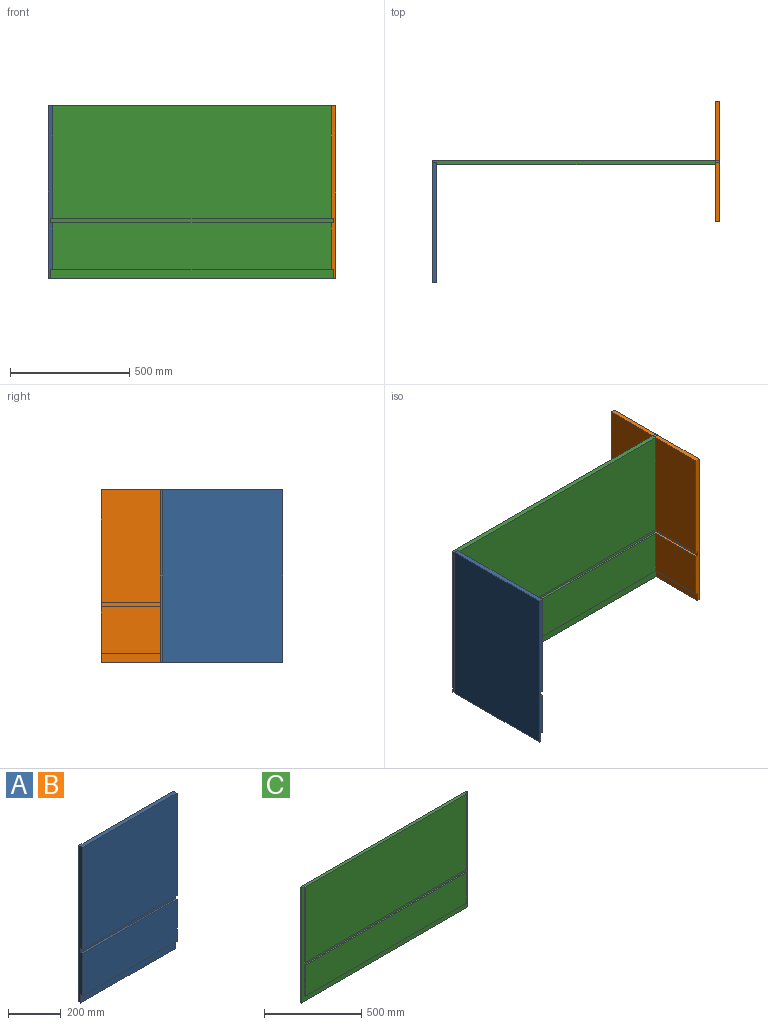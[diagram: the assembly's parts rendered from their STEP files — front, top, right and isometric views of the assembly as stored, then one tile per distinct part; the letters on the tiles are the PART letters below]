
ASSEMBLY  parts=3 mates=4
PART A: 12 faces, bbox 504.8x19.1x723.9 mm
  f0: plane 504.83x9.53mm, normal (0,0,-1), area 4808.5mm2, adj f3,f5,f6,f11
  f1: plane 504.83x473.08mm, normal (0,-1,0), area 238820.1mm2, adj f3,f4,f5,f8
  f2: plane 504.83x193.68mm, normal (0,-1,0), area 97772mm2, adj f3,f5,f7,f10
  f3: plane 723.9x19.05mm, normal (1,0,0), area 13245.9mm2, adj f0,f1,f2,f4,f6,f7,f8,f9
  f4: plane 504.83x19.05mm, normal (0,0,1), area 9616.9mm2, adj f1,f3,f5,f6
  f5: plane 723.9x19.05mm, normal (-1,0,0), area 13245.9mm2, adj f0,f1,f2,f4,f6,f7,f8,f9
  f6: plane 723.9x504.83mm, normal (0,1,0), area 365442.8mm2, adj f0,f3,f4,f5
  f7: plane 504.83x9.53mm, normal (0,0,1), area 4808.5mm2, adj f2,f3,f5,f9
  f8: plane 504.83x9.53mm, normal (0,0,-1), area 4808.5mm2, adj f1,f3,f5,f9
  f9: plane 504.83x19.05mm, normal (0,-1,0), area 9616.9mm2, adj f3,f5,f7,f8
  f10: plane 504.83x9.53mm, normal (0,0,-1), area 4808.5mm2, adj f2,f3,f5,f11
  f11: plane 504.83x38.1mm, normal (0,-1,0), area 19233.8mm2, adj f0,f3,f5,f10
PART B: same geometry as A
PART C: 15 faces, bbox 1206.5x19.1x723.9 mm
  f0: plane 723.9x9.53mm, normal (1,0,0), area 6895.1mm2, adj f2,f3,f5,f13
  f1: plane 723.9x9.53mm, normal (-1,0,0), area 6895.1mm2, adj f2,f3,f5,f13
  f2: plane 1206.5x9.53mm, normal (0,0,-1), area 11491.9mm2, adj f0,f1,f5,f13
  f3: plane 1206.5x19.05mm, normal (0,0,1), area 22620.9mm2, adj f0,f1,f4,f5,f9,f11,f13
  f4: plane 1168.4x473.08mm, normal (0,-1,0), area 552740.8mm2, adj f3,f9,f10,f11
  f5: plane 1206.5x723.9mm, normal (0,1,0), area 873385.3mm2, adj f0,f1,f2,f3
  f6: plane 1168.4x9.53mm, normal (0,0,-1), area 11129mm2, adj f7,f12,f13,f14
  f7: plane 193.68x9.53mm, normal (-1,0,0), area 1844.8mm2, adj f6,f8,f13,f14
  f8: plane 1168.4x9.53mm, normal (0,0,1), area 11129mm2, adj f7,f12,f13,f14
  f9: plane 473.08x9.53mm, normal (1,0,0), area 4506mm2, adj f3,f4,f10,f13
  f10: plane 1168.4x9.53mm, normal (0,0,-1), area 11129mm2, adj f4,f9,f11,f13
  f11: plane 473.08x9.53mm, normal (-1,0,0), area 4506mm2, adj f3,f4,f10,f13
  f12: plane 193.68x9.53mm, normal (1,0,0), area 1844.8mm2, adj f6,f8,f13,f14
  f13: plane 1206.5x723.9mm, normal (0,-1,0), area 94354.6mm2, adj f0,f1,f2,f3,f6,f7,f8,f9
  f14: plane 1168.4x193.68mm, normal (0,-1,0), area 226289.9mm2, adj f6,f7,f8,f12
PLACE A rot(axis=(0,0,1),90deg) t=(-684.3,99.39,-213.83)mm
PLACE B rot(axis=(0,0,-1),90deg) t=(522.2,356.57,-213.83)mm
PLACE C t=(-81.05,351.8,-213.83)mm fixed
MATE planar C.f3 <-> A.f4  axis (0,0,1) through (-81.05,351.88,148.12)mm
MATE fastened B.f6 <-> C.f0  axis (1,0,0) through (522.2,356.57,-213.83)mm
MATE planar A.f6 <-> C.f1  axis (-1,0,0) through (-684.3,99.39,-213.83)mm
MATE planar C.f13 <-> A.f3  axis (0,-1,0) through (-81.05,351.8,-404.07)mm
